# Revit family: C1000R
name_source: partatom
category: Mechanical Equipment
revit_build: Autodesk Revit 2015 (Build: 20140223_1515(x64)
units: mm (PartAtom-declared; Revit-internal decimal feet)

## types (3) — shared parameters
D = 140 mm  [stored 0.459318 ft]
Flow = No
Noise output dB(A) @3m high = 55 mm  [stored 0.180446 ft]
Noise output dB(A) @3m low = 50
Noise output dB(A) @3m med = 53
URL = http://www.thermoscreens.com
boundary work space box = No
center X = 605 mm
center Y = 177 mm
drop rod 1 = 25 mm  [stored 0.082021 ft]
drop rod 2 = 22 mm
flange length = 1209 mm  [stored 3.96654 ft]
flange width = 353 mm  [stored 1.15814 ft]
holes distance = 33 mm  [stored 0.108268 ft]
unit center X = 590 mm
unit center Y = 151 mm
unit length = 1179 mm  [stored 3.86811 ft]
unit width = 301 mm  [stored 0.987533 ft]
wall to water hole dis = 188 mm

## per-type parameters (varying)
| type | Heat output (kW) | Loading (A) per phase | Max velocity (m/s) | Supply (50hz) | Weight | boundary work space | max air volume (m3/h) |
| C1000ER | 4.5/9 | 13.7 | 9 | 400V 3P&N | 20kg | 500 mm  [stored 1.64042 ft] | 1190 |
| C1000WR 82/71 | 6 | 0.7 | 8.5 | 230V 1P&N | 22kg | 409 mm | 1120 |
| C1000AR | 0 | 0.7 | 9 | 230V 1P&N | 19KG | 409 mm | 1190 |

note: [stored X ft] marks values corroborated as IEEE doubles in the binary element streams (Revit-internal decimal feet)

## geometry (parser evidence)
native form markers: Sweep x2
no freeform markers — native parametric forms only
